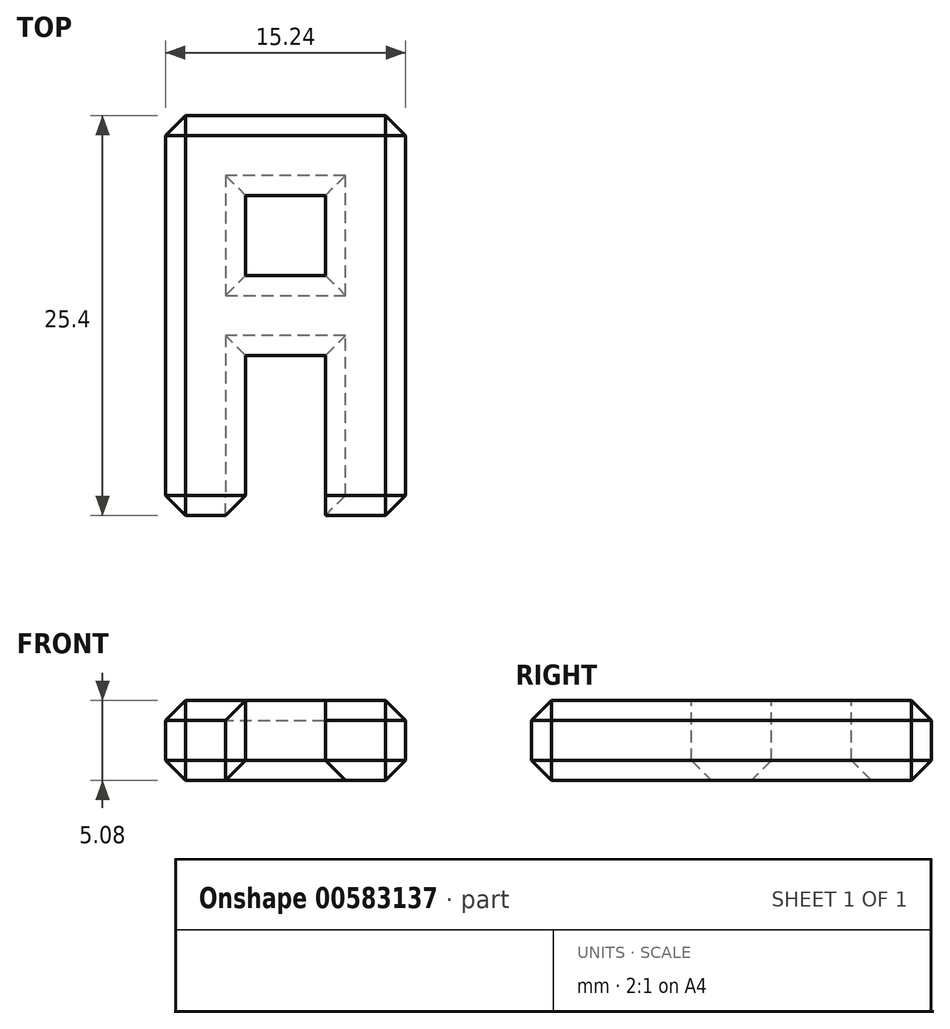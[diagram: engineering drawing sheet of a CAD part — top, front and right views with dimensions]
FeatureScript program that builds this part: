
annotation { "Feature Type Name" : "Feature", "Feature Type Description" : "" }
export const myFeature = defineFeature(function(context is Context, id is Id, definition is map)
    precondition{}
    {
        {
            var Q0;
            Q0=qCreatedBy(makeId("Top.planeOp"),FACE);
            var sketch = newSketch(context, id + "F0", { "sketchPlane" : qUnion([Q0])});
            skLineSegment(sketch, "E0.bottom", {"start": v(7.62, 12.7) * mm, "end": v(-7.62, 12.7) * mm});
            skLineSegment(sketch, "E0.top", {"start": v(7.62, -12.7) * mm, "end": v(-7.62, -12.7) * mm});
            skLineSegment(sketch, "E0.left", {"start": v(7.62, 12.7) * mm, "end": v(7.62, -12.7) * mm});
            skLineSegment(sketch, "E0.right", {"start": v(-7.62, 12.7) * mm, "end": v(-7.62, -12.7) * mm});
            skPoint(sketch, "E0.middle", {"position": v(0, 0) * mm});
            skSolve(sketch);
        }
        {
            var Q0;
            Q0=makeQuery(id+"F0.imprint","IMPRINT",FACE,{"disambiguationData":[TD([[makeQuery(id+"F0.imprint","IMPRINT",EDGE,{"derivedFrom":sQuery(id+"F0.wireOp",EDGE,"E0.bottom")}),1.0]])]});
            extrude(context, id + "F1", {"entities" : qUnion([Q0]), "depth" : 5.08 * mm, "offsetDistance" : 25.4 * mm});
        }
        {
            var Q0;
            Q0=makeQuery(id+"F1.opExtrude","CAP_FACE",FACE,{"disambiguationData":[OSD([sQuery(id+"F0.wireOp",EDGE,"E0.bottom"),sQuery(id+"F0.wireOp",EDGE,"E0.top"),sQuery(id+"F0.wireOp",EDGE,"E0.left"),sQuery(id+"F0.wireOp",EDGE,"E0.right")])],"isStart":false});
            var sketch = newSketch(context, id + "F2", { "sketchPlane" : qUnion([Q0])});
            skLineSegment(sketch, "E1.bottom", {"start": v(-2.54, -12.7) * mm, "end": v(2.54, -12.7) * mm});
            skLineSegment(sketch, "E1.top", {"start": v(-2.54, -2.54) * mm, "end": v(2.54, -2.54) * mm});
            skLineSegment(sketch, "E1.left", {"start": v(-2.54, -12.7) * mm, "end": v(-2.54, -2.54) * mm});
            skLineSegment(sketch, "E1.right", {"start": v(2.54, -12.7) * mm, "end": v(2.54, -2.54) * mm});
            skLineSegment(sketch, "E2.bottom", {"start": v(-2.54, 7.62) * mm, "end": v(2.54, 7.62) * mm});
            skLineSegment(sketch, "E2.top", {"start": v(-2.54, 2.54) * mm, "end": v(2.54, 2.54) * mm});
            skLineSegment(sketch, "E2.left", {"start": v(-2.54, 7.62) * mm, "end": v(-2.54, 2.54) * mm});
            skLineSegment(sketch, "E2.right", {"start": v(2.54, 7.62) * mm, "end": v(2.54, 2.54) * mm});
            skSolve(sketch);
        }
        {
            var Q0;
            Q0=makeQuery(id+"F2.imprint","IMPRINT",FACE,{"disambiguationData":[TD([[makeQuery(id+"F2.imprint","IMPRINT",EDGE,{"derivedFrom":sQuery(id+"F2.wireOp",EDGE,"E2.bottom")}),-1.0]])]});
            var Q1;
            Q1=makeQuery(id+"F2.imprint","IMPRINT",FACE,{"disambiguationData":[TD([[makeQuery(id+"F2.imprint","IMPRINT",EDGE,{"derivedFrom":sQuery(id+"F2.wireOp",EDGE,"E1.bottom")}),-1.0]])]});
            extrude(context, id + "F3", {"entities" : qUnion([Q0, Q1]), "operationType" : NewBodyOperationType.REMOVE, "oppositeDirection" : true, "depth" : 5.08 * mm, "offsetDistance" : 25.4 * mm});
        }
        {
            var Q0;
            Q0=makeQuery(id+"F3.boolean.opBoolean","COPY",EDGE,{"derivedFrom":makeQuery(id+"F3.opExtrude","CAP_EDGE",EDGE,{"disambiguationData":[OSD([sQuery(id+"F2.wireOp",EDGE,"E2.bottom")])],"isStart":true})});
            var Q1;
            Q1=makeQuery(id+"F3.boolean.opBoolean","COPY",EDGE,{"derivedFrom":makeQuery(id+"F3.opExtrude","CAP_EDGE",EDGE,{"disambiguationData":[OSD([sQuery(id+"F2.wireOp",EDGE,"E2.bottom")])],"isStart":false})});
            var Q2;
            Q2=makeQuery(id+"F3.boolean.opBoolean","COPY",EDGE,{"derivedFrom":makeQuery(id+"F3.opExtrude","CAP_EDGE",EDGE,{"disambiguationData":[OSD([sQuery(id+"F2.wireOp",EDGE,"E2.left")])],"isStart":true})});
            var Q3;
            Q3=makeQuery(id+"F3.boolean.opBoolean","COPY",EDGE,{"derivedFrom":makeQuery(id+"F3.opExtrude","CAP_EDGE",EDGE,{"disambiguationData":[OSD([sQuery(id+"F2.wireOp",EDGE,"E2.top")])],"isStart":true})});
            var Q4;
            Q4=makeQuery(id+"F3.boolean.opBoolean","COPY",EDGE,{"derivedFrom":makeQuery(id+"F3.opExtrude","CAP_EDGE",EDGE,{"disambiguationData":[OSD([sQuery(id+"F2.wireOp",EDGE,"E2.right")])],"isStart":true})});
            var Q5;
            Q5=makeQuery(id+"F3.boolean.opBoolean","COPY",EDGE,{"derivedFrom":makeQuery(id+"F3.opExtrude","CAP_EDGE",EDGE,{"disambiguationData":[OSD([sQuery(id+"F2.wireOp",EDGE,"E1.top")])],"isStart":true})});
            var Q6;
            Q6=makeQuery(id+"F3.boolean.opBoolean","COPY",EDGE,{"derivedFrom":makeQuery(id+"F3.opExtrude","CAP_EDGE",EDGE,{"disambiguationData":[OSD([sQuery(id+"F2.wireOp",EDGE,"E1.left")])],"isStart":true})});
            var Q7;
            Q7=makeQuery(id+"F3.boolean.opBoolean","COPY",EDGE,{"derivedFrom":makeQuery(id+"F3.opExtrude","CAP_EDGE",EDGE,{"disambiguationData":[OSD([sQuery(id+"F2.wireOp",EDGE,"E1.right")])],"isStart":true})});
            var Q8;
            Q8=makeQuery(id+"F1.opExtrude","CAP_EDGE",EDGE,{"disambiguationData":[OSD([sQuery(id+"F0.wireOp",EDGE,"E0.right")])],"isStart":false});
            var Q9;
            Q9=makeQuery(id+"F1.opExtrude","CAP_EDGE",EDGE,{"disambiguationData":[OSD([sQuery(id+"F0.wireOp",EDGE,"E0.left")])],"isStart":false});
            var Q10;
            Q10=makeQuery(id+"F1.opExtrude","CAP_EDGE",EDGE,{"disambiguationData":[OSD([sQuery(id+"F0.wireOp",EDGE,"E0.bottom")])],"isStart":false});
            var Q11;
            {var subQ0=sQuery(id+"F0.wireOp",EDGE,"E0.right");var subQ1=sQuery(id+"F0.wireOp",EDGE,"E0.top");Q11=makeQuery(id+"F3.boolean.opBoolean","SPLIT",EDGE,{"disambiguationData":[TD([makeQuery(id+"F1.opExtrude","SWEPT_FACE",FACE,{"disambiguationData":[OSD([subQ0])]})])],"derivedFrom":makeQuery(id+"F1.opExtrude","CAP_EDGE",EDGE,{"disambiguationData":[OSD([subQ1])],"isStart":false})});}
            var Q12;
            {var subQ0=sQuery(id+"F0.wireOp",EDGE,"E0.left");var subQ1=sQuery(id+"F0.wireOp",EDGE,"E0.top");Q12=makeQuery(id+"F3.boolean.opBoolean","SPLIT",EDGE,{"disambiguationData":[TD([makeQuery(id+"F1.opExtrude","SWEPT_FACE",FACE,{"disambiguationData":[OSD([subQ0])]})])],"derivedFrom":makeQuery(id+"F1.opExtrude","CAP_EDGE",EDGE,{"disambiguationData":[OSD([subQ1])],"isStart":false})});}
            var Q13;
            Q13=makeQuery(id+"F3.boolean.opBoolean","COPY",EDGE,{"derivedFrom":makeQuery(id+"F3.opExtrude","SWEPT_EDGE",EDGE,{"disambiguationData":[OSD([sQuery(id+"F0.wireOp",EDGE,"E0.top"),sQuery(id+"F2.wireOp",EDGE,"E1.bottom"),sQuery(id+"F2.wireOp",EDGE,"E1.left")])]})});
            var Q14;
            Q14=makeQuery(id+"F3.boolean.opBoolean","COPY",EDGE,{"derivedFrom":makeQuery(id+"F3.opExtrude","SWEPT_EDGE",EDGE,{"disambiguationData":[OSD([sQuery(id+"F0.wireOp",EDGE,"E0.top"),sQuery(id+"F2.wireOp",EDGE,"E1.bottom"),sQuery(id+"F2.wireOp",EDGE,"E1.right")])]})});
            var Q15;
            Q15=makeQuery(id+"F1.opExtrude","SWEPT_EDGE",EDGE,{"disambiguationData":[OSD([sQuery(id+"F0.wireOp",EDGE,"E0.top"),sQuery(id+"F0.wireOp",EDGE,"E0.left")])]});
            var Q16;
            Q16=makeQuery(id+"F1.opExtrude","SWEPT_EDGE",EDGE,{"disambiguationData":[OSD([sQuery(id+"F0.wireOp",EDGE,"E0.top"),sQuery(id+"F0.wireOp",EDGE,"E0.right")])]});
            var Q17;
            {var subQ0=sQuery(id+"F0.wireOp",EDGE,"E0.right");var subQ1=sQuery(id+"F0.wireOp",EDGE,"E0.top");Q17=makeQuery(id+"F3.boolean.opBoolean","SPLIT",EDGE,{"disambiguationData":[TD([makeQuery(id+"F1.opExtrude","SWEPT_FACE",FACE,{"disambiguationData":[OSD([subQ0])]})])],"derivedFrom":makeQuery(id+"F1.opExtrude","CAP_EDGE",EDGE,{"disambiguationData":[OSD([subQ1])],"isStart":true})});}
            var Q18;
            {var subQ0=sQuery(id+"F0.wireOp",EDGE,"E0.left");var subQ1=sQuery(id+"F0.wireOp",EDGE,"E0.top");Q18=makeQuery(id+"F3.boolean.opBoolean","SPLIT",EDGE,{"disambiguationData":[TD([makeQuery(id+"F1.opExtrude","SWEPT_FACE",FACE,{"disambiguationData":[OSD([subQ0])]})])],"derivedFrom":makeQuery(id+"F1.opExtrude","CAP_EDGE",EDGE,{"disambiguationData":[OSD([subQ1])],"isStart":true})});}
            var Q19;
            Q19=makeQuery(id+"F1.opExtrude","CAP_EDGE",EDGE,{"disambiguationData":[OSD([sQuery(id+"F0.wireOp",EDGE,"E0.right")])],"isStart":true});
            var Q20;
            Q20=makeQuery(id+"F1.opExtrude","CAP_EDGE",EDGE,{"disambiguationData":[OSD([sQuery(id+"F0.wireOp",EDGE,"E0.left")])],"isStart":true});
            var Q21;
            Q21=makeQuery(id+"F3.boolean.opBoolean","COPY",EDGE,{"derivedFrom":makeQuery(id+"F3.opExtrude","CAP_EDGE",EDGE,{"disambiguationData":[OSD([sQuery(id+"F2.wireOp",EDGE,"E1.left")])],"isStart":false})});
            var Q22;
            Q22=makeQuery(id+"F1.opExtrude","CAP_FACE",FACE,{"disambiguationData":[OSD([sQuery(id+"F0.wireOp",EDGE,"E0.bottom"),sQuery(id+"F0.wireOp",EDGE,"E0.top"),sQuery(id+"F0.wireOp",EDGE,"E0.left"),sQuery(id+"F0.wireOp",EDGE,"E0.right")])],"isStart":true});
            var Q23;
            Q23=makeQuery(id+"F1.opExtrude","SWEPT_EDGE",EDGE,{"disambiguationData":[OSD([sQuery(id+"F0.wireOp",EDGE,"E0.bottom"),sQuery(id+"F0.wireOp",EDGE,"E0.right")])]});
            var Q24;
            Q24=makeQuery(id+"F1.opExtrude","SWEPT_EDGE",EDGE,{"disambiguationData":[OSD([sQuery(id+"F0.wireOp",EDGE,"E0.bottom"),sQuery(id+"F0.wireOp",EDGE,"E0.left")])]});
            chamfer(context, id + "F4", {"entities" : qUnion([Q0, Q1, Q2, Q3, Q4, Q5, Q6, Q7, Q8, Q9, Q10, Q11, Q12, Q13, Q14, Q15, Q16, Q17, Q18, Q19, Q20, Q21, Q22, Q23, Q24]), "width" : 1.27 * mm, "tangentPropagation" : true});
        }
    });
